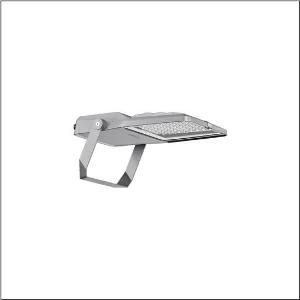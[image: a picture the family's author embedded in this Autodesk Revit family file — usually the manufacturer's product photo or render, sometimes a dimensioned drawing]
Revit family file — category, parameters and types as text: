
# Revit family: floodlight_fl_21_mini___pl52_5xa7776c2d1a_43f3
name_source: partatom
category: Lighting Fixtures
units: mm (PartAtom-declared; Revit-internal decimal feet)

## family parameters
Cut with Voids When Loaded = No
Host = Face
Light Source = No
Part Type = Normal
Room Calculation Point = No
Round Connector Dimension = Use Diameter
Shared = No

## types (1)
- --- (1 x LED, 12190 lm, 89 W, 3000K)
    Apparent Load = 89 VA
    CIE Flux Codes = 26 60 98 100 100
    Color Rendering = 70
    Color Temperature = 3000K
    Default Elevation = 1800 mm
    Description = Floodlight FL 21 mini, floodlight, primary light control with lens, of PMMA, primary optical cover: protective disc, of toughened safety glass, transparent, light distribution: PL52, light emission: direct distribution, installation type: surface-mounted, LED, High Power LED, rated luminous flux: 12.190lm, luminous efficacy: 137lm/W, light colour: 730, colour temperature: 3000K, control: flexible luminous flux parameterisation, time-dependent luminous flux control, constant luminous flux control, overheat protection, presetting dimming logarithmic, with terminal, 6-pole, mains connection: 220..240V, AC, 50/60Hz, start of lifetime: 89W, end of service life: 94W, reduction: 43W, luminaire housing, of diecast aluminium, powder-coated, Siteco® metallic grey (DB 702S), corrosivity category C5 mid according to DIN EN ISO 12944, sealing non-destructively replaceable, mounting bracket, of steel, galvanised, powder-coated, Siteco® metallic grey (DB 702S), Smart Interface below and above, protection rating (complete): IP66, insulation class (complete): insulation class II (safety insulation), certification: CE, ENEC, VDE, protection symbol: D, impact resistance: IK08, permissible operating ambient temperature: -40..+40°C, permissible operating ambient temperature for outdoor applications: -40..+50°C, standard: DIN EN 12944, LABS conformity tested according to VDMA 24364:2018-05, packaging unit: 1 piece

Light Distribution: PL52
    Height = 70 mm
    Lamp = 1 x LED
    Lamp Light Flux = 12190 lm
    Lamp Power = 89 W
    Lamp count = 1
    Length = 485 mm
    Luminous efficacy = 137 lm/W
    Manufacturer = Siteco
    ModVariant = No
    Model = 5XA7776C2D1A
    Number of Poles = 1
    OnlyDefault = Yes
    Power Factor = 1
    Product Name = Floodlight FL 21 mini | PL52
    Product group = floodlight | pylon annexe
    ProductGroupID = 6200
    Protection Class = Protection class II
    Protection Degree = IP 66
    RLX_Detail_Level = 1
    RLX_Emergency_Light_Flux = 0 lm
    RLX_Emergency_Type = 0
    RLX_Emergency_Type_DB = No
    RlxData = <blob elided: 95997 chars, md5=561cca1d>
    Socket = socket
    Standby Power = 0 W
    System Light Flux = 12190 lm
    System Power = 89 W
    Type Comments = factory setting: luminous flux: 100 % | dim-lin: 254 | 456 mA
    Type Image = l_1006845.jpg
    URL = http://relux.com
    VarID = @adj_113441
    Voltage = 0 V
    Weight = 0.00 kg
    Width = 337 mm

## geometry (parser evidence)
native form markers: Blend x4, Sweep x13
no freeform markers — native parametric forms only
